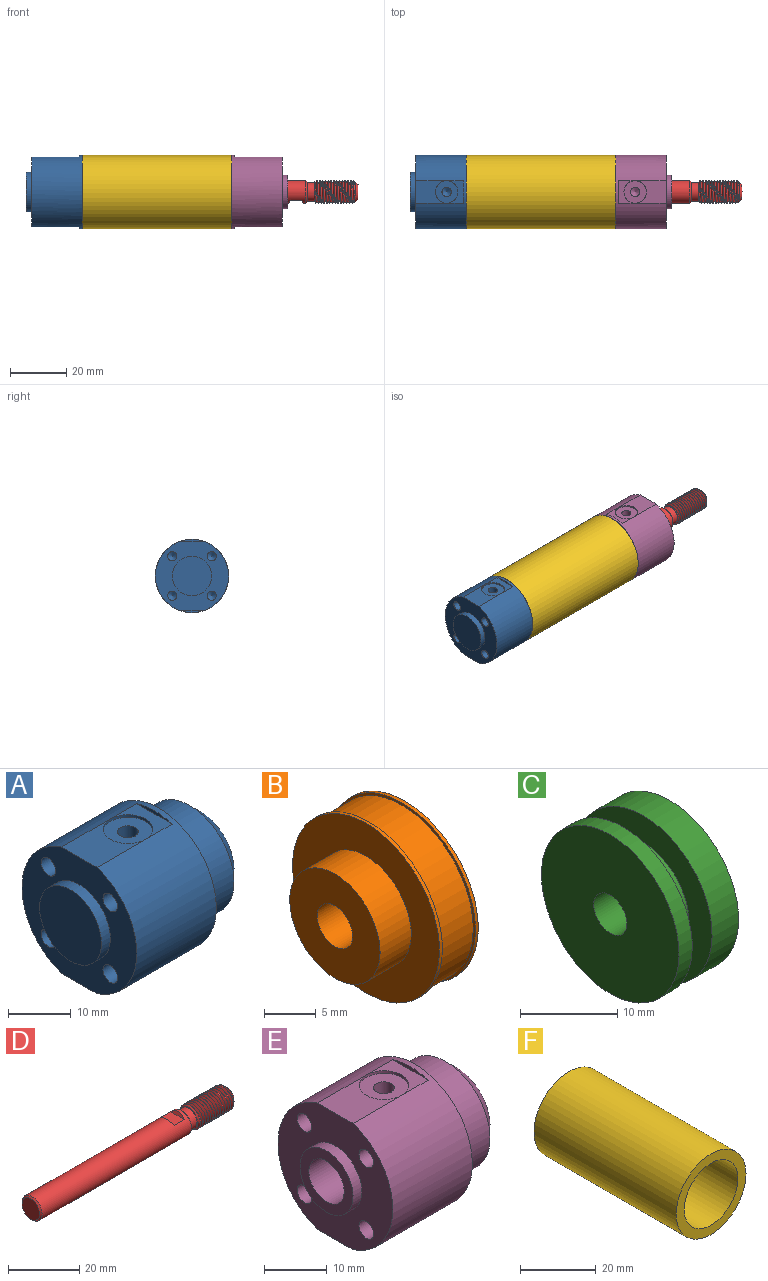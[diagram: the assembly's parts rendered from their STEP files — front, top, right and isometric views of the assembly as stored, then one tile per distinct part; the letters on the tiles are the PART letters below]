
ASSEMBLY  parts=6 mates=5
PART A: 31 faces, bbox 29.5x26x26 mm
  f0: cylinder r=10mm len=20mm, axis (-1,0,0), area 439.8mm2, adj f4,f30
  f1: plane 11x8mm, normal (0,0,1), area 62.9mm2, adj f2,f3,f19
  f2: cylinder r=13mm len=26mm, axis (1,0,0), area 1193.7mm2, adj f1,f3,f4,f15,f16,f17,f18,f23
  f3: plane 26x24.74mm, normal (-1,0,0), area 336mm2, adj f1,f2,f5,f7,f9,f11,f13,f15
  f4: plane 26x26mm, normal (1,0,0), area 216.8mm2, adj f0,f2
  f5: cylinder r=7mm len=14mm, axis (1,0,0), area 88mm2, adj f3,f6
  f6: plane 14x14mm, normal (-1,0,0), area 153.9mm2, adj f5
  f7: cylinder r=1.65mm len=7mm, axis (-1,0,0), area 72.6mm2, adj f3,f8
  f8: cone r=0mm half-angle=59deg, axis (-1,0,0), area 10mm2, adj f7
  f9: cylinder r=1.65mm len=7mm, axis (-1,0,0), area 72.6mm2, adj f3,f10
  f10: cone r=0mm half-angle=59deg, axis (-1,0,0), area 10mm2, adj f9
  f11: cylinder r=1.65mm len=7mm, axis (-1,0,0), area 72.6mm2, adj f3,f12
  f12: cone r=0mm half-angle=59deg, axis (-1,0,0), area 10mm2, adj f11
  f13: cylinder r=1.65mm len=7mm, axis (-1,0,0), area 72.6mm2, adj f3,f14
  f14: cone r=0mm half-angle=59deg, axis (-1,0,0), area 10mm2, adj f13
  f15: plane 17x8mm, normal (0,0,-1), area 85.8mm2, adj f2,f3,f16,f23
  f16: plane 8x0.63mm, normal (-1,0,0), area 3.4mm2, adj f2,f15
  f17: plane 8x6mm, normal (0,0,1), area 22.9mm2, adj f2,f18,f19
  f18: plane 8x0.63mm, normal (-1,0,0), area 3.4mm2, adj f2,f17
  f19: cylinder r=4mm len=8mm, axis (0,0,1), area 12.6mm2, adj f1,f17,f20
  f20: plane 8x8mm, normal (0,0,1), area 41.7mm2, adj f19,f22
  f21: cone r=0mm half-angle=59deg, axis (0,0,1), area 10mm2, adj f22
  f22: cylinder r=1.65mm len=4.7mm, axis (0,0,1), area 48.7mm2, adj f20,f21
  f23: cylinder r=4mm len=8mm, axis (0,0,-1), area 12.6mm2, adj f2,f15,f24
  f24: plane 8x8mm, normal (0,0,-1), area 41.7mm2, adj f23,f26
  f25: cone r=0mm half-angle=59deg, axis (0,0,-1), area 10mm2, adj f26
  f26: cylinder r=1.65mm len=4.7mm, axis (0,0,-1), area 48.7mm2, adj f24,f25
  f27: plane 15x15mm, normal (1,0,0), area 98.2mm2, adj f29,f30
  f28: plane 10x10mm, normal (1,0,0), area 78.5mm2, adj f29
  f29: cylinder r=5mm len=10mm, axis (1,0,0), area 298.5mm2, adj f27,f28
  f30: cone r=7.5mm half-angle=45deg, axis (-1,0,0), area 194.4mm2, adj f0,f27
PART B: 12 faces, bbox 9.5x20x20 mm
  f0: cylinder r=9.7mm len=19.4mm, axis (-1,0,0), area 274.3mm2, adj f1,f11
  f1: plane 20x20mm, normal (1,0,0), area 18.6mm2, adj f0,f2
  f2: cylinder r=10mm len=20mm, axis (-1,0,0), area 24.5mm2, adj f1,f3
  f3: plane 20x20mm, normal (-1,0,0), area 195.3mm2, adj f2,f4
  f4: cylinder r=6.15mm len=12.3mm, axis (-1,0,0), area 163.6mm2, adj f3,f5
  f5: plane 12.3x12.3mm, normal (-1,0,0), area 100.7mm2, adj f4,f6
  f6: cylinder r=2.4mm len=5.19mm, axis (-1,0,0), area 78.3mm2, adj f5,f7
  f7: plane 10x10mm, normal (1,0,0), area 60.4mm2, adj f6,f8
  f8: cylinder r=5mm len=10mm, axis (-1,0,0), area 135.7mm2, adj f7,f9
  f9: plane 20x20mm, normal (1,0,0), area 235.6mm2, adj f8,f10
  f10: cylinder r=10mm len=20mm, axis (-1,0,0), area 24.5mm2, adj f9,f11
  f11: plane 20x20mm, normal (-1,0,0), area 18.6mm2, adj f0,f10
PART C: 10 faces, bbox 8.7x20x20 mm
  f0: cylinder r=2.4mm len=4.8mm, axis (-1,0,0), area 72.4mm2, adj f1,f9
  f1: plane 12.3x12.3mm, normal (1,0,0), area 100.7mm2, adj f0,f2
  f2: cylinder r=6.15mm len=12.3mm, axis (-1,0,0), area 148.8mm2, adj f1,f3
  f3: plane 20x20mm, normal (1,0,0), area 195.3mm2, adj f2,f4
  f4: cylinder r=10mm len=20mm, axis (-1,0,0), area 241.9mm2, adj f3,f5
  f5: plane 20x20mm, normal (-1,0,0), area 175.6mm2, adj f4,f6
  f6: cylinder r=6.64mm len=13.28mm, axis (-1,0,0), area 120.2mm2, adj f5,f7
  f7: plane 20x20mm, normal (1,0,0), area 175.6mm2, adj f6,f8
  f8: cylinder r=10mm len=20mm, axis (-1,0,0), area 120.6mm2, adj f7,f9
  f9: plane 20x20mm, normal (-1,0,0), area 296.1mm2, adj f0,f8
PART D: 19 faces, bbox 78.4x8x9.2 mm
  f0: plane 7x7mm, normal (-1,0,0), area 5.3mm2, adj f4,f16
  f1: cylinder r=4mm len=59.43mm, axis (1,0,0), area 1466.1mm2, adj f7,f8,f9,f14,f15,f17,f18
  f2: plane 5x5mm, normal (1,0,0), area 19.6mm2, adj f13
  f3: cylinder r=4mm len=13.5mm, axis (1,0,0), area 2.5mm2, adj f10,f11,f12,f13,f16
  f4: cylinder r=3.25mm len=6.5mm, axis (1,0,0), area 51.1mm2, adj f0,f5
  f5: plane 7x7mm, normal (1,0,0), area 5.3mm2, adj f4,f17
  f6: plane 7x7mm, normal (-1,0,0), area 38.5mm2, adj f18
  f7: plane 5.29x0mm, normal (1,0,0), area 0mm2, adj f1,f9,f15
  f8: plane 5.29x0mm, normal (-1,0,0), area 0mm2, adj f1,f9,f14
  f9: plane 5.29x4mm, normal (0,0,1), area 21.2mm2, adj f1,f7,f8
  f10: bspline ~15.12x9.24mm, area 281.9mm2, adj f3,f11,f12,f13
  f11: plane 0.78x0.63mm, normal (0,0,-1), area 0.2mm2, adj f3,f10,f12,f16
  f12: bspline ~15.12x9.24mm, area 289.3mm2, adj f3,f10,f11,f13,f16
  f13: cone r=2.5mm half-angle=45deg, axis (-1,0,0), area 31.7mm2, adj f2,f3,f10,f12
  f14: plane 5.28x1mm, normal (-0.87,0,0.5), area 4.2mm2, adj f1,f8
  f15: plane 5.28x1mm, normal (0.87,0,0.5), area 4.2mm2, adj f1,f7
  f16: cone r=4mm half-angle=45deg, axis (1,0,0), area 10.6mm2, adj f0,f3,f11,f12
  f17: cone r=3.5mm half-angle=45deg, axis (-1,0,0), area 16.7mm2, adj f1,f5
  f18: cone r=4mm half-angle=45deg, axis (1,0,0), area 16.7mm2, adj f1,f6
PART E: 32 faces, bbox 29.5x26x26 mm
  f0: plane 11x8mm, normal (0,0,1), area 62.9mm2, adj f1,f2,f24
  f1: cylinder r=13mm len=26mm, axis (1,0,0), area 1193.7mm2, adj f0,f2,f5,f20,f21,f22,f23,f28
  f2: plane 26x24.74mm, normal (-1,0,0), area 376.9mm2, adj f0,f1,f6,f8,f10,f12,f14,f20
  f3: plane 10x10mm, normal (1,0,0), area 28.3mm2, adj f4,f16
  f4: cylinder r=4mm len=20mm, axis (1,0,0), area 502.7mm2, adj f3,f7
  f5: plane 26x26mm, normal (1,0,0), area 216.8mm2, adj f1,f17
  f6: cylinder r=6mm len=12mm, axis (1,0,0), area 75.4mm2, adj f2,f7
  f7: plane 12x12mm, normal (-1,0,0), area 62.8mm2, adj f4,f6
  f8: cylinder r=1.65mm len=7mm, axis (-1,0,0), area 72.6mm2, adj f2,f9
  f9: cone r=0mm half-angle=59deg, axis (-1,0,0), area 10mm2, adj f8
  f10: cylinder r=1.65mm len=7mm, axis (-1,0,0), area 72.6mm2, adj f2,f11
  f11: cone r=0mm half-angle=59deg, axis (-1,0,0), area 10mm2, adj f10
  f12: cylinder r=1.65mm len=7mm, axis (-1,0,0), area 72.6mm2, adj f2,f13
  f13: cone r=0mm half-angle=59deg, axis (-1,0,0), area 10mm2, adj f12
  f14: cylinder r=1.65mm len=7mm, axis (-1,0,0), area 72.6mm2, adj f2,f15
  f15: cone r=0mm half-angle=59deg, axis (-1,0,0), area 10mm2, adj f14
  f16: cylinder r=5mm len=10mm, axis (-1,0,0), area 298.5mm2, adj f3,f18
  f17: cylinder r=10mm len=20mm, axis (-1,0,0), area 439.8mm2, adj f5,f19
  f18: plane 15x15mm, normal (1,0,0), area 98.2mm2, adj f16,f19
  f19: cone r=7.5mm half-angle=45deg, axis (-1,0,0), area 194.4mm2, adj f17,f18
  f20: plane 17x8mm, normal (0,0,-1), area 85.8mm2, adj f1,f2,f21,f28
  f21: plane 8x0.63mm, normal (-1,0,0), area 3.4mm2, adj f1,f20
  f22: plane 8x6mm, normal (0,0,1), area 22.9mm2, adj f1,f23,f24
  f23: plane 8x0.63mm, normal (-1,0,0), area 3.4mm2, adj f1,f22
  f24: cylinder r=4mm len=8mm, axis (0,0,1), area 12.6mm2, adj f0,f22,f25
  f25: plane 8x8mm, normal (0,0,1), area 41.7mm2, adj f24,f27
  f26: cone r=0mm half-angle=59deg, axis (0,0,1), area 10mm2, adj f27
  f27: cylinder r=1.65mm len=4.7mm, axis (0,0,1), area 48.7mm2, adj f25,f26
  f28: cylinder r=4mm len=8mm, axis (0,0,-1), area 12.6mm2, adj f1,f20,f29
  f29: plane 8x8mm, normal (0,0,-1), area 41.7mm2, adj f28,f31
  f30: cone r=0mm half-angle=59deg, axis (0,0,-1), area 10mm2, adj f31
  f31: cylinder r=1.65mm len=4.7mm, axis (0,0,-1), area 48.7mm2, adj f29,f30
PART F: 4 faces, bbox 26x53x26 mm
  f0: cylinder r=10mm len=53mm, axis (0,1,0), area 3330.1mm2, adj f2,f3
  f1: cylinder r=13mm len=53mm, axis (0,1,0), area 4329.1mm2, adj f2,f3
  f2: plane 26x26mm, normal (0,-1,0), area 216.8mm2, adj f0,f1
  f3: plane 26x26mm, normal (0,1,0), area 216.8mm2, adj f0,f1
PLACE A t=(15.66,-82.29,52.17)mm
PLACE B t=(29.96,-82.29,52.17)mm
PLACE C t=(30.16,-82.29,52.17)mm
PLACE D rot(axis=(1,0,0),180deg) t=(35.15,-82.29,52.17)mm
PLACE E rot(axis=(0,0,1),180deg) t=(68.66,-82.29,52.17)mm
PLACE F rot(axis=(-0.58,-0.58,-0.58),120deg) t=(68.66,-81.68,52.01)mm
MATE fastened E.f16 <-> F.f0  axis (1,0,0) through (68.66,-82.29,52.17)mm
MATE fastened A.f30 <-> F.f0  axis (-1,0,0) through (15.66,-82.29,52.17)mm
MATE fastened C.f0 <-> B.f0  axis (1,0,0) through (29.96,-82.29,52.17)mm
MATE slider C.f0 <-> F.f0  axis (-1,0,0) through (25.16,-82.29,52.17)mm
MATE fastened D.f1 <-> B.f0  axis (-1,0,0) through (35.15,-82.29,52.17)mm
